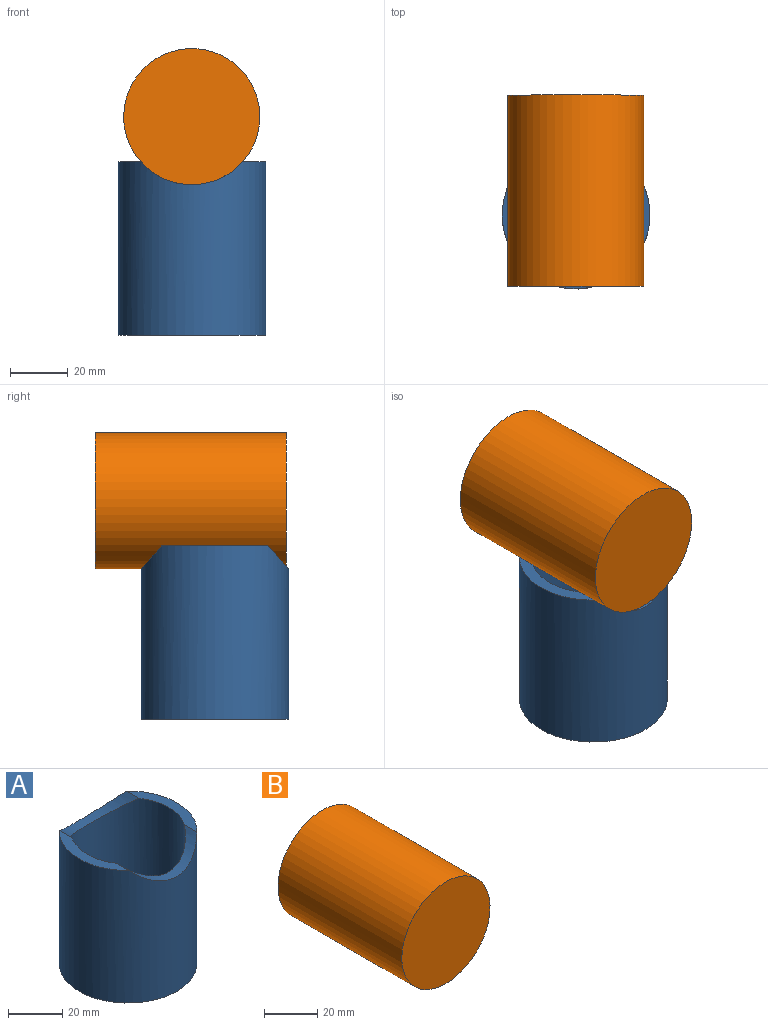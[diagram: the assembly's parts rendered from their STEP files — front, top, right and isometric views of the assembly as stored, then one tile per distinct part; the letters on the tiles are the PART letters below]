
ASSEMBLY  parts=2 mates=1
PART A: 7 faces, bbox 51x51x60 mm
  f0: plane 36.58x7.73mm, normal (0,0,1), area 140.1mm2, adj f1,f3,f5,f6
  f1: cylinder r=21.25mm len=60mm, axis (0,0,-1), area 7580.7mm2, adj f0,f2,f4,f5,f6
  f2: plane 51x51mm, normal (0,0,-1), area 624.2mm2, adj f1,f3
  f3: cylinder r=25.5mm len=60mm, axis (0,0,-1), area 9197.6mm2, adj f0,f2,f4,f5,f6
  f4: plane 36.99x7.94mm, normal (0,0,1), area 142.8mm2, adj f1,f3,f5,f6
  f5: cylinder r=23.5mm len=35.33mm, axis (0,-1,0), area 196.1mm2, adj f0,f1,f3,f4
  f6: cylinder r=23.5mm len=35.33mm, axis (0,-1,0), area 196.1mm2, adj f0,f1,f3,f4
PART B: 3 faces, bbox 47x66x47 mm
  f0: cylinder r=23.5mm len=66mm, axis (0,1,0), area 9745.2mm2, adj f1,f2
  f1: plane 47x47mm, normal (0,-1,0), area 1734.9mm2, adj f0
  f2: plane 47x47mm, normal (0,1,0), area 1734.9mm2, adj f0
PLACE A t=(-123,-71.53,-97.12)mm
PLACE B t=(-123.11,-30.19,-21.62)mm
MATE cylindrical A.f5 <-> B.f0  axis (0,-1,0) through (-123.11,-90.13,-21.62)mm
